# Revit family: HC_Valve_Radiator_MEPcontent_Oventrop_AV 9_Reversed Angle Pattern
name_source: partatom
category: Pipe Accessories
revit_build: Autodesk Revit 2015 (Build: 20140223_1515(x64)
units: mm (PartAtom-declared; Revit-internal decimal feet)

## types (3) — shared parameters
Article Description = Thermostatic radiator valve, reversed angle pattern
Brass = Color RGB 168-128-048
Cast Iron = Color RGB 140-140-140
Content Supplier URL = www.mepcontent.eu
Custom = No
Description = Thermostatic radiator valve, reversed angle pattern
EMCS Version = 2.0
ETIM Article Class = EC010136
Family Version = 10.14
IFCExportAs = IfcValveType
IFCExportType = REGULATING
Kvs Value = 0.67
MEPcontent Class = VALVE_RADIATOR
Manufacturer = Oventrop
Manufacturer URL = http://www.oventrop.de
Pressure Stage = 10.0 Pa
Product Line = Oventrop
Revit Version = 2015
URL = www.stabiplan.com
Use Nominal Diameter = Yes
Valve Body Radius1 = 13 mm  [stored 0.0426509 ft]
Valve Insert Diameter = 30 mm  [stored 0.0984252 ft]

## per-type parameters (varying)
- DN 10: Blend Position=7 mm  [stored 0.0229659 ft]; Bottom Height=22 mm  [stored 0.0721785 ft]; Bottom Part Radius=10 mm  [stored 0.0328084 ft]; Connection Outer Radius=8.6 mm; Connection Piece Radius=8 mm  [stored 0.0262467 ft]; Copper Connection Diameter=12 mm  [stored 0.0393701 ft]; Copper Connection Radius=6 mm  [stored 0.019685 ft]; GTIN=04026755407358; Height=42.5 mm; Horizontal Nut Diameter=27 mm  [stored 0.0885827 ft]; Horizontal Nut Height=13.5 mm  [stored 0.0442913 ft]; Horizontal Nut Position=20 mm  [stored 0.0656168 ft]; Length=109 mm; Manufacturer Art. No.=1183903; Middle Section Radius=8 mm  [stored 0.0262467 ft]; Profile Depth=12 mm  [stored 0.0393701 ft]; Reference Line Radius=3.5 mm  [stored 0.0114829 ft]; Rind Height=13.5 mm  [stored 0.0442913 ft]; Ring Position=14 mm  [stored 0.0459318 ft]; Ring Radius=13.5 mm  [stored 0.0442913 ft]; Thread Connection Diameter=9.5 mm  [stored 0.031168 ft]; Thread Connection Nominal Diameter=9.5 mm  [stored 0.031168 ft]; Thread Connection Nominal Radius=4.75 mm  [stored 0.015584 ft]; Thread Connection Outer Diameter=17.2 mm; Valve Body Height=21.5 mm  [stored 0.0705381 ft]; Valve Body Radius2=10.5 mm  [stored 0.0344488 ft]; Valve Position=57 mm; Vertical Nut Diameter=25.4 mm  [stored 0.0833333 ft]; Vertical Nut Height=13 mm  [stored 0.0426509 ft]
- DN 15: Blend Position=7 mm  [stored 0.0229659 ft]; Bottom Height=26 mm; Bottom Part Radius=11.5 mm  [stored 0.0377297 ft]; Connection Outer Radius=10.65 mm  [stored 0.0349409 ft]; Connection Piece Radius=10.5 mm  [stored 0.0344488 ft]; Copper Connection Diameter=15 mm  [stored 0.0492126 ft]; Copper Connection Radius=7.5 mm  [stored 0.0246063 ft]; GTIN=04026755407365; Height=50.5 mm; Horizontal Nut Diameter=30 mm  [stored 0.0984252 ft]; Horizontal Nut Height=15 mm  [stored 0.0492126 ft]; Horizontal Nut Position=23 mm  [stored 0.0754593 ft]; Length=114 mm; Manufacturer Art. No.=1183904; Middle Section Radius=9 mm  [stored 0.0295276 ft]; Profile Depth=16 mm  [stored 0.0524934 ft]; Reference Line Radius=4.5 mm  [stored 0.0147638 ft]; Rind Height=13 mm  [stored 0.0426509 ft]; Ring Position=13 mm  [stored 0.0426509 ft]; Ring Radius=15 mm  [stored 0.0492126 ft]; Thread Connection Diameter=12.7 mm  [stored 0.0416667 ft]; Thread Connection Nominal Diameter=12.7 mm  [stored 0.0416667 ft]; Thread Connection Nominal Radius=6.35 mm  [stored 0.0208333 ft]; Thread Connection Outer Diameter=21.3 mm  [stored 0.0698819 ft]; Valve Body Height=22 mm  [stored 0.0721785 ft]; Valve Body Radius2=12 mm  [stored 0.0393701 ft]; Valve Position=56 mm; Vertical Nut Diameter=30 mm  [stored 0.0984252 ft]; Vertical Nut Height=14 mm  [stored 0.0459318 ft]
- DN 20: Blend Position=5 mm  [stored 0.0164042 ft]; Bottom Height=37 mm  [stored 0.121391 ft]; Bottom Part Radius=13 mm  [stored 0.0426509 ft]; Connection Outer Radius=13.45 mm; Connection Piece Radius=13 mm  [stored 0.0426509 ft]; Copper Connection Diameter=22 mm  [stored 0.0721785 ft]; Copper Connection Radius=11 mm  [stored 0.0360892 ft]; GTIN=04026755407372; Height=65.5 mm; Horizontal Nut Diameter=37 mm  [stored 0.121391 ft]; Horizontal Nut Height=16.5 mm  [stored 0.0541339 ft]; Horizontal Nut Position=24.5 mm  [stored 0.0803806 ft]; Length=120 mm; Manufacturer Art. No.=1183906; Middle Section Radius=13 mm  [stored 0.0426509 ft]; Profile Depth=20 mm  [stored 0.0656168 ft]; Reference Line Radius=4.5 mm  [stored 0.0147638 ft]; Rind Height=13 mm  [stored 0.0426509 ft]; Ring Position=13 mm  [stored 0.0426509 ft]; Ring Radius=15 mm  [stored 0.0492126 ft]; Thread Connection Diameter=19 mm  [stored 0.062336 ft]; Thread Connection Nominal Diameter=19 mm  [stored 0.062336 ft]; Thread Connection Nominal Radius=9.5 mm  [stored 0.031168 ft]; Thread Connection Outer Diameter=26.9 mm; Valve Body Height=19 mm  [stored 0.062336 ft]; Valve Body Radius2=14 mm  [stored 0.0459318 ft]; Valve Position=53 mm; Vertical Nut Diameter=37 mm  [stored 0.121391 ft]; Vertical Nut Height=20 mm  [stored 0.0656168 ft]

note: column(s) folded — value = type name in every type: Article Type, Model

note: [stored X ft] marks values corroborated as IEEE doubles in the binary element streams (Revit-internal decimal feet)

## geometry (parser evidence)
native form markers: Sweep x8
no freeform markers — native parametric forms only
